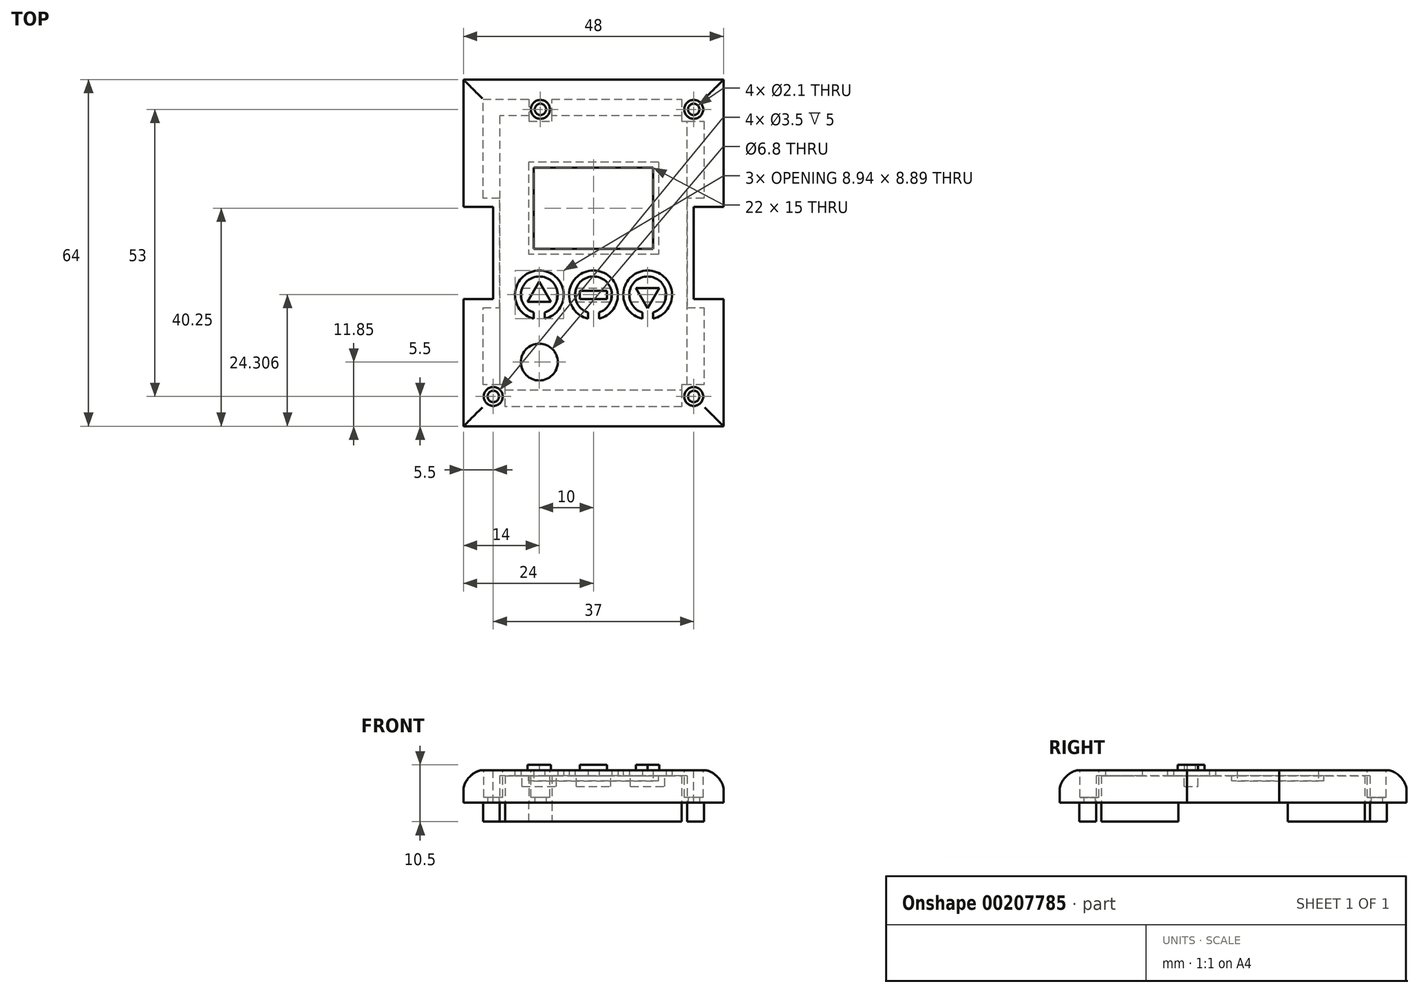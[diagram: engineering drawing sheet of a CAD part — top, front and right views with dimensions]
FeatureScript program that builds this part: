
annotation { "Feature Type Name" : "Feature", "Feature Type Description" : "" }
export const myFeature = defineFeature(function(context is Context, id is Id, definition is map)
    precondition{}
    {
        {
            var Q0;
            Q0=qCreatedBy(makeId("Top.planeOp"),FACE);
            var sketch = newSketch(context, id + "F0", { "sketchPlane" : qUnion([Q0])});
            skLineSegment(sketch, "E0.bottom", {"start": v(24, 32) * mm, "end": v(-24, 32) * mm});
            skLineSegment(sketch, "E0.top", {"start": v(24, -32) * mm, "end": v(-24, -32) * mm});
            skLineSegment(sketch, "E0.left", {"start": v(24, 32) * mm, "end": v(24, -32) * mm});
            skLineSegment(sketch, "E0.right", {"start": v(-24, 32) * mm, "end": v(-24, -32) * mm});
            skPoint(sketch, "E0.middle", {"position": v(0, 0) * mm});
            skSolve(sketch);
        }
        {
            var Q0;
            Q0 = qSketchRegion(id + "F0", true);
            extrude(context, id + "F1", {"entities" : qUnion([Q0]), "depth" : 6 * mm});
        }
        {
            var Q0;
            Q0=makeQuery(id+"F1.opExtrude","CAP_FACE",FACE,{"disambiguationData":[OSD([sQuery(id+"F0.wireOp",EDGE,"E0.bottom"),sQuery(id+"F0.wireOp",EDGE,"E0.top"),sQuery(id+"F0.wireOp",EDGE,"E0.left"),sQuery(id+"F0.wireOp",EDGE,"E0.right")])],"isStart":false});
            var sketch = newSketch(context, id + "F2", { "sketchPlane" : qUnion([Q0])});
            skLineSegment(sketch, "E1.bottom", {"start": v(-24, 8.5) * mm, "end": v(-18.5, 8.5) * mm});
            skLineSegment(sketch, "E1.top", {"start": v(-24, -8.5) * mm, "end": v(-18.5, -8.5) * mm});
            skLineSegment(sketch, "E1.left", {"start": v(-24, 8.5) * mm, "end": v(-24, -8.5) * mm});
            skLineSegment(sketch, "E1.right", {"start": v(-18.5, 8.5) * mm, "end": v(-18.5, -8.5) * mm});
            skPoint(sketch, "E1.middle", {"position": v(-21.25, 0) * mm});
            skLineSegment(sketch, "E2.bottom", {"start": v(24, 8.5) * mm, "end": v(18.5, 8.5) * mm});
            skLineSegment(sketch, "E2.top", {"start": v(24, -8.5) * mm, "end": v(18.5, -8.5) * mm});
            skLineSegment(sketch, "E2.left", {"start": v(24, 8.5) * mm, "end": v(24, -8.5) * mm});
            skLineSegment(sketch, "E2.right", {"start": v(18.5, 8.5) * mm, "end": v(18.5, -8.5) * mm});
            skPoint(sketch, "E2.middle", {"position": v(21.25, 0) * mm});
            skSolve(sketch);
        }
        {
            var Q0;
            Q0 = qSketchRegion(id + "F2", true);
            extrude(context, id + "F3", {"entities" : qUnion([Q0]), "operationType" : NewBodyOperationType.REMOVE, "endBound" : BoundingType.THROUGH_ALL, "oppositeDirection" : true, "depth" : 25 * mm});
        }
        {
            var Q0;
            Q0=makeQuery(id+"F1.opExtrude","CAP_FACE",FACE,{"disambiguationData":[OSD([sQuery(id+"F0.wireOp",EDGE,"E0.bottom"),sQuery(id+"F0.wireOp",EDGE,"E0.top"),sQuery(id+"F0.wireOp",EDGE,"E0.left"),sQuery(id+"F0.wireOp",EDGE,"E0.right")])],"isStart":true});
            var sketch = newSketch(context, id + "F4", { "sketchPlane" : qUnion([Q0])});
            skLineSegment(sketch, "E3", {"start": v(-20.4, -28.4) * mm, "end": v(-11.9, -28.4) * mm});
            skLineSegment(sketch, "E4", {"start": v(-11.9, -28.4) * mm, "end": v(-11.9, -24.3) * mm});
            skLineSegment(sketch, "E5", {"start": v(-11.9, -24.3) * mm, "end": v(-7.7, -24.3) * mm});
            skLineSegment(sketch, "E6", {"start": v(-7.7, -24.3) * mm, "end": v(-7.7, -28.4) * mm});
            skLineSegment(sketch, "E7", {"start": v(-7.7, -28.4) * mm, "end": v(16.3, -28.4) * mm});
            skLineSegment(sketch, "E8", {"start": v(16.3, -28.4) * mm, "end": v(16.3, -24.3) * mm});
            skLineSegment(sketch, "E9", {"start": v(16.3, -24.3) * mm, "end": v(20.4, -24.3) * mm});
            skLineSegment(sketch, "E10", {"start": v(20.4, -24.3) * mm, "end": v(20.4, -10.1) * mm});
            skLineSegment(sketch, "E11", {"start": v(20.4, -10.1) * mm, "end": v(15.5, -10.1) * mm});
            skLineSegment(sketch, "E12", {"start": v(15.5, -10.1) * mm, "end": v(15.5, 10.1) * mm});
            skLineSegment(sketch, "E13", {"start": v(15.5, 10.1) * mm, "end": v(20.4, 10.1) * mm});
            skLineSegment(sketch, "E14", {"start": v(20.4, 10.1) * mm, "end": v(20.4, 24.3) * mm});
            skLineSegment(sketch, "E15", {"start": v(20.4, 24.3) * mm, "end": v(16.3, 24.3) * mm});
            skLineSegment(sketch, "E16", {"start": v(16.3, 24.3) * mm, "end": v(16.3, 28.4) * mm});
            skLineSegment(sketch, "E17", {"start": v(16.3, 28.4) * mm, "end": v(-16.3, 28.4) * mm});
            skLineSegment(sketch, "E18", {"start": v(-16.3, 28.4) * mm, "end": v(-16.3, 24.3) * mm});
            skLineSegment(sketch, "E19", {"start": v(-16.3, 24.3) * mm, "end": v(-20.4, 24.3) * mm});
            skLineSegment(sketch, "E20", {"start": v(-20.4, 24.3) * mm, "end": v(-20.4, 10.1) * mm});
            skLineSegment(sketch, "E21", {"start": v(-20.4, 10.1) * mm, "end": v(-15.5, 10.1) * mm});
            skLineSegment(sketch, "E22", {"start": v(-15.5, 10.1) * mm, "end": v(-15.5, -10.1) * mm});
            skLineSegment(sketch, "E23", {"start": v(-15.5, -10.1) * mm, "end": v(-20.4, -10.1) * mm});
            skLineSegment(sketch, "E24", {"start": v(-20.4, -10.1) * mm, "end": v(-20.4, -28.4) * mm});
            skSolve(sketch);
        }
        {
            var Q0;
            Q0 = qSketchRegion(id + "F4", true);
            extrude(context, id + "F5", {"entities" : qUnion([Q0]), "operationType" : NewBodyOperationType.ADD, "depth" : 3.5 * mm});
        }
        {
            var Q0;
            Q0=makeQuery(id+"F5.opExtrude","CAP_FACE",FACE,{"disambiguationData":[OSD([sQuery(id+"F4.wireOp",EDGE,"E3"),sQuery(id+"F4.wireOp",EDGE,"E4"),sQuery(id+"F4.wireOp",EDGE,"E5"),sQuery(id+"F4.wireOp",EDGE,"E6"),sQuery(id+"F4.wireOp",EDGE,"E7"),sQuery(id+"F4.wireOp",EDGE,"E8"),sQuery(id+"F4.wireOp",EDGE,"E9"),sQuery(id+"F4.wireOp",EDGE,"E10"),sQuery(id+"F4.wireOp",EDGE,"E11"),sQuery(id+"F4.wireOp",EDGE,"E12"),sQuery(id+"F4.wireOp",EDGE,"E13"),sQuery(id+"F4.wireOp",EDGE,"E14"),sQuery(id+"F4.wireOp",EDGE,"E15"),sQuery(id+"F4.wireOp",EDGE,"E16"),sQuery(id+"F4.wireOp",EDGE,"E17"),sQuery(id+"F4.wireOp",EDGE,"E18"),sQuery(id+"F4.wireOp",EDGE,"E19"),sQuery(id+"F4.wireOp",EDGE,"E20"),sQuery(id+"F4.wireOp",EDGE,"E21"),sQuery(id+"F4.wireOp",EDGE,"E22"),sQuery(id+"F4.wireOp",EDGE,"E23"),sQuery(id+"F4.wireOp",EDGE,"E24")])],"isStart":false});
            var sketch = newSketch(context, id + "F6", { "sketchPlane" : qUnion([Q0])});
            skLineSegment(sketch, "E25", {"start": v(-16.3, 24.3) * mm, "end": v(-16.3, 25.3) * mm});
            skLineSegment(sketch, "E26", {"start": v(-16.3, 25.3) * mm, "end": v(16.3, 25.3) * mm});
            skLineSegment(sketch, "E27", {"start": v(16.3, 25.3) * mm, "end": v(16.3, 24.3) * mm});
            skLineSegment(sketch, "E28", {"start": v(16.3, 24.3) * mm, "end": v(17.3, 24.3) * mm});
            skPoint(sketch, "E29.endSnap0", {"position": v(17.95, 10.1) * mm});
            skLineSegment(sketch, "E30", {"start": v(17.3, 24.3) * mm, "end": v(17.3, -24.3) * mm});
            skLineSegment(sketch, "E31", {"start": v(17.3, -24.3) * mm, "end": v(16.3, -24.3) * mm});
            skLineSegment(sketch, "E32", {"start": v(16.3, -24.3) * mm, "end": v(16.3, -25.3) * mm});
            skLineSegment(sketch, "E33", {"start": v(16.3, -25.3) * mm, "end": v(-7.7, -25.3) * mm});
            skLineSegment(sketch, "E34", {"start": v(-7.7, -25.3) * mm, "end": v(-7.7, -24.3) * mm});
            skLineSegment(sketch, "E35", {"start": v(-7.7, -24.3) * mm, "end": v(-11.9, -24.3) * mm});
            skLineSegment(sketch, "E36", {"start": v(-11.9, -24.3) * mm, "end": v(-11.9, -25.3) * mm});
            skLineSegment(sketch, "E37", {"start": v(-11.9, -25.3) * mm, "end": v(-17.3, -25.3) * mm});
            skLineSegment(sketch, "E38", {"start": v(-17.3, -25.3) * mm, "end": v(-17.3, 24.3) * mm});
            skLineSegment(sketch, "E39", {"start": v(-17.3, 24.3) * mm, "end": v(-16.3, 24.3) * mm});
            skSolve(sketch);
        }
        {
            var Q0;
            Q0 = qSketchRegion(id + "F6", true);
            extrude(context, id + "F7", {"entities" : qUnion([Q0]), "operationType" : NewBodyOperationType.REMOVE, "oppositeDirection" : true, "depth" : 8.5 * mm});
        }
        {
            var Q0;
            Q0=makeQuery(id+"F1.opExtrude","CAP_FACE",FACE,{"disambiguationData":[OSD([sQuery(id+"F0.wireOp",EDGE,"E0.bottom"),sQuery(id+"F0.wireOp",EDGE,"E0.top"),sQuery(id+"F0.wireOp",EDGE,"E0.left"),sQuery(id+"F0.wireOp",EDGE,"E0.right")])],"isStart":true});
            var sketch = newSketch(context, id + "F8", { "sketchPlane" : qUnion([Q0])});
            skCircle(sketch, "E40", {"center": v(-18.5, 26.5) * mm, "radius": 1.05 * mm});
            skCircle(sketch, "E41", {"center": v(18.5, 26.5) * mm, "radius": 1.05 * mm});
            skCircle(sketch, "E42", {"center": v(18.5, -26.5) * mm, "radius": 1.05 * mm});
            skCircle(sketch, "E43", {"center": v(-9.8, -26.5) * mm, "radius": 1.05 * mm});
            skPoint(sketch, "E43.centerSnap0", {"position": v(-9.8, -24.3) * mm});
            skSolve(sketch);
        }
        {
            var Q0;
            Q0 = qSketchRegion(id + "F8", true);
            extrude(context, id + "F9", {"entities" : qUnion([Q0]), "operationType" : NewBodyOperationType.REMOVE, "endBound" : BoundingType.THROUGH_ALL, "oppositeDirection" : true, "depth" : 25 * mm});
        }
        {
            var Q0;
            Q0=makeQuery(id+"F1.opExtrude","CAP_FACE",FACE,{"disambiguationData":[OSD([sQuery(id+"F0.wireOp",EDGE,"E0.bottom"),sQuery(id+"F0.wireOp",EDGE,"E0.top"),sQuery(id+"F0.wireOp",EDGE,"E0.left"),sQuery(id+"F0.wireOp",EDGE,"E0.right")])],"isStart":false});
            var sketch = newSketch(context, id + "F10", { "sketchPlane" : qUnion([Q0])});
            skCircle(sketch, "E44", {"center": v(-9.8, 26.5) * mm, "radius": 1.75 * mm});
            skCircle(sketch, "E45", {"center": v(18.5, 26.5) * mm, "radius": 1.75 * mm});
            skCircle(sketch, "E46", {"center": v(18.5, -26.5) * mm, "radius": 1.75 * mm});
            skCircle(sketch, "E47", {"center": v(-18.5, -26.5) * mm, "radius": 1.75 * mm});
            skSolve(sketch);
        }
        {
            var Q0;
            Q0 = qSketchRegion(id + "F10", true);
            extrude(context, id + "F11", {"entities" : qUnion([Q0]), "operationType" : NewBodyOperationType.REMOVE, "oppositeDirection" : true, "depth" : 5 * mm});
        }
        {
            var Q0;
            Q0=makeQuery(id+"F7.boolean.opBoolean","COPY",FACE,{"derivedFrom":makeQuery(id+"F7.opExtrude","CAP_FACE",FACE,{"disambiguationData":[OSD([sQuery(id+"F6.wireOp",EDGE,"E25"),sQuery(id+"F6.wireOp",EDGE,"E26"),sQuery(id+"F6.wireOp",EDGE,"E27"),sQuery(id+"F6.wireOp",EDGE,"E28"),sQuery(id+"F6.wireOp",EDGE,"E30"),sQuery(id+"F6.wireOp",EDGE,"E31"),sQuery(id+"F6.wireOp",EDGE,"E32"),sQuery(id+"F6.wireOp",EDGE,"E33"),sQuery(id+"F6.wireOp",EDGE,"E34"),sQuery(id+"F6.wireOp",EDGE,"E35"),sQuery(id+"F6.wireOp",EDGE,"E36"),sQuery(id+"F6.wireOp",EDGE,"E37"),sQuery(id+"F6.wireOp",EDGE,"E38"),sQuery(id+"F6.wireOp",EDGE,"E39")])],"isStart":false})});
            var sketch = newSketch(context, id + "F12", { "sketchPlane" : qUnion([Q0])});
            skLineSegment(sketch, "E48.bottom", {"start": v(11, -0.75) * mm, "end": v(-11, -0.75) * mm});
            skLineSegment(sketch, "E48.top", {"start": v(11, -15.75) * mm, "end": v(-11, -15.75) * mm});
            skLineSegment(sketch, "E48.left", {"start": v(11, -0.75) * mm, "end": v(11, -15.75) * mm});
            skLineSegment(sketch, "E48.right", {"start": v(-11, -0.75) * mm, "end": v(-11, -15.75) * mm});
            skPoint(sketch, "E48.middle", {"position": v(0, -8.25) * mm});
            skSolve(sketch);
        }
        {
            var Q0;
            Q0 = qSketchRegion(id + "F12", true);
            extrude(context, id + "F13", {"entities" : qUnion([Q0]), "operationType" : NewBodyOperationType.REMOVE, "endBound" : BoundingType.THROUGH_ALL, "oppositeDirection" : true, "depth" : 25 * mm});
        }
        {
            var Q0;
            Q0=makeQuery(id+"F7.boolean.opBoolean","COPY",FACE,{"derivedFrom":makeQuery(id+"F7.opExtrude","CAP_FACE",FACE,{"disambiguationData":[OSD([sQuery(id+"F6.wireOp",EDGE,"E25"),sQuery(id+"F6.wireOp",EDGE,"E26"),sQuery(id+"F6.wireOp",EDGE,"E27"),sQuery(id+"F6.wireOp",EDGE,"E28"),sQuery(id+"F6.wireOp",EDGE,"E30"),sQuery(id+"F6.wireOp",EDGE,"E31"),sQuery(id+"F6.wireOp",EDGE,"E32"),sQuery(id+"F6.wireOp",EDGE,"E33"),sQuery(id+"F6.wireOp",EDGE,"E34"),sQuery(id+"F6.wireOp",EDGE,"E35"),sQuery(id+"F6.wireOp",EDGE,"E36"),sQuery(id+"F6.wireOp",EDGE,"E37"),sQuery(id+"F6.wireOp",EDGE,"E38"),sQuery(id+"F6.wireOp",EDGE,"E39")])],"isStart":false})});
            var sketch = newSketch(context, id + "F14", { "sketchPlane" : qUnion([Q0])});
            skArc(sketch, "E49", {"start": v(-1, 11) * mm, "mid": v(0, 4.35) * mm, "end": v(1, 11) * mm});
            skArc(sketch, "E50", {"start": v(-1, 12.14) * mm, "mid": v(0, 3.25) * mm, "end": v(1, 12.14) * mm});
            skLineSegment(sketch, "E51", {"start": v(-1, 12.14) * mm, "end": v(-1, 11) * mm});
            skLineSegment(sketch, "E52", {"start": v(1, 12.14) * mm, "end": v(1, 11) * mm});
            skArc(sketch, "E53", {"start": v(11, 11) * mm, "mid": v(10, 4.35) * mm, "end": v(9, 11) * mm});
            skArc(sketch, "E54", {"start": v(11, 12.14) * mm, "mid": v(10, 3.25) * mm, "end": v(9, 12.14) * mm});
            skLineSegment(sketch, "E55", {"start": v(11, 11) * mm, "end": v(11, 12.14) * mm});
            skLineSegment(sketch, "E56", {"start": v(9, 11) * mm, "end": v(9, 12.14) * mm});
            skArc(sketch, "E57", {"start": v(-9, 11) * mm, "mid": v(-10, 4.35) * mm, "end": v(-11, 11) * mm});
            skArc(sketch, "E58", {"start": v(-9, 12.14) * mm, "mid": v(-10, 3.25) * mm, "end": v(-11, 12.14) * mm});
            skLineSegment(sketch, "E59", {"start": v(-9, 11) * mm, "end": v(-9, 12.14) * mm});
            skLineSegment(sketch, "E60", {"start": v(-11, 12.14) * mm, "end": v(-11, 11) * mm});
            skSolve(sketch);
        }
        {
            var Q0;
            Q0 = qSketchRegion(id + "F14", true);
            extrude(context, id + "F15", {"entities" : qUnion([Q0]), "operationType" : NewBodyOperationType.REMOVE, "endBound" : BoundingType.THROUGH_ALL, "oppositeDirection" : true, "depth" : 25 * mm});
        }
        {
            var Q0;
            Q0=makeQuery(id+"F7.boolean.opBoolean","COPY",FACE,{"derivedFrom":makeQuery(id+"F7.opExtrude","CAP_FACE",FACE,{"disambiguationData":[OSD([sQuery(id+"F6.wireOp",EDGE,"E25"),sQuery(id+"F6.wireOp",EDGE,"E26"),sQuery(id+"F6.wireOp",EDGE,"E27"),sQuery(id+"F6.wireOp",EDGE,"E28"),sQuery(id+"F6.wireOp",EDGE,"E30"),sQuery(id+"F6.wireOp",EDGE,"E31"),sQuery(id+"F6.wireOp",EDGE,"E32"),sQuery(id+"F6.wireOp",EDGE,"E33"),sQuery(id+"F6.wireOp",EDGE,"E34"),sQuery(id+"F6.wireOp",EDGE,"E35"),sQuery(id+"F6.wireOp",EDGE,"E36"),sQuery(id+"F6.wireOp",EDGE,"E37"),sQuery(id+"F6.wireOp",EDGE,"E38"),sQuery(id+"F6.wireOp",EDGE,"E39")])],"isStart":false})});
            var sketch = newSketch(context, id + "F16", { "sketchPlane" : qUnion([Q0])});
            skLineSegment(sketch, "E61.bottom", {"start": v(-13.16, 9) * mm, "end": v(-6.84, 9) * mm});
            skLineSegment(sketch, "E61.top", {"start": v(-13.16, 6.5) * mm, "end": v(-6.84, 6.5) * mm});
            skLineSegment(sketch, "E61.left", {"start": v(-13.16, 9) * mm, "end": v(-13.16, 6.5) * mm});
            skLineSegment(sketch, "E61.right", {"start": v(-6.84, 9) * mm, "end": v(-6.84, 6.5) * mm});
            skLineSegment(sketch, "E62.bottom", {"start": v(-3.16, 9) * mm, "end": v(3.16, 9) * mm});
            skLineSegment(sketch, "E62.top", {"start": v(-3.16, 6.5) * mm, "end": v(3.16, 6.5) * mm});
            skLineSegment(sketch, "E62.left", {"start": v(-3.16, 9) * mm, "end": v(-3.16, 6.5) * mm});
            skLineSegment(sketch, "E62.right", {"start": v(3.16, 9) * mm, "end": v(3.16, 6.5) * mm});
            skLineSegment(sketch, "E63.bottom", {"start": v(6.84, 9) * mm, "end": v(13.16, 9) * mm});
            skLineSegment(sketch, "E63.top", {"start": v(6.84, 6.5) * mm, "end": v(13.16, 6.5) * mm});
            skLineSegment(sketch, "E63.left", {"start": v(6.84, 9) * mm, "end": v(6.84, 6.5) * mm});
            skLineSegment(sketch, "E63.right", {"start": v(13.16, 9) * mm, "end": v(13.16, 6.5) * mm});
            skSolve(sketch);
        }
        {
            var Q0;
            Q0 = qSketchRegion(id + "F16", true);
            extrude(context, id + "F17", {"entities" : qUnion([Q0]), "operationType" : NewBodyOperationType.ADD, "depth" : 2 * mm});
        }
        {
            var Q0;
            Q0=makeQuery(id+"F1.opExtrude","CAP_FACE",FACE,{"disambiguationData":[OSD([sQuery(id+"F0.wireOp",EDGE,"E0.bottom"),sQuery(id+"F0.wireOp",EDGE,"E0.top"),sQuery(id+"F0.wireOp",EDGE,"E0.left"),sQuery(id+"F0.wireOp",EDGE,"E0.right")])],"isStart":false});
            var sketch = newSketch(context, id + "F18", { "sketchPlane" : qUnion([Q0])});
            skCircle(sketch, "E64.cCircle", {"center": v(10, -7.75) * mm, "radius": 2.5 * mm, "construction": true});
            skLineSegment(sketch, "E64.0", {"start": v(10, -10.25) * mm, "end": v(7.83, -6.5) * mm});
            skLineSegment(sketch, "E64.1", {"start": v(7.83, -6.5) * mm, "end": v(12.17, -6.5) * mm});
            skLineSegment(sketch, "E64.2", {"start": v(12.17, -6.5) * mm, "end": v(10, -10.25) * mm});
            skCircle(sketch, "E65.cCircle", {"center": v(-10, -7.75) * mm, "radius": 2.5 * mm, "construction": true});
            skLineSegment(sketch, "E65.0", {"start": v(-12.17, -9) * mm, "end": v(-10, -5.25) * mm});
            skLineSegment(sketch, "E65.1", {"start": v(-10, -5.25) * mm, "end": v(-7.83, -9) * mm});
            skLineSegment(sketch, "E65.2", {"start": v(-7.83, -9) * mm, "end": v(-12.17, -9) * mm});
            skLineSegment(sketch, "E66.bottom", {"start": v(-2.5, -8.5) * mm, "end": v(2.5, -8.5) * mm});
            skLineSegment(sketch, "E66.top", {"start": v(-2.5, -7) * mm, "end": v(2.5, -7) * mm});
            skLineSegment(sketch, "E66.left", {"start": v(-2.5, -8.5) * mm, "end": v(-2.5, -7) * mm});
            skLineSegment(sketch, "E66.right", {"start": v(2.5, -8.5) * mm, "end": v(2.5, -7) * mm});
            skPoint(sketch, "E66.middle", {"position": v(0, -7.75) * mm});
            skSolve(sketch);
        }
        {
            var Q0;
            Q0 = qSketchRegion(id + "F18", true);
            extrude(context, id + "F19", {"entities" : qUnion([Q0]), "operationType" : NewBodyOperationType.ADD, "depth" : 1 * mm});
        }
        {
            var Q0;
            Q0=makeQuery(id+"F7.boolean.opBoolean","COPY",FACE,{"derivedFrom":makeQuery(id+"F7.opExtrude","CAP_FACE",FACE,{"disambiguationData":[OSD([sQuery(id+"F6.wireOp",EDGE,"E25"),sQuery(id+"F6.wireOp",EDGE,"E26"),sQuery(id+"F6.wireOp",EDGE,"E27"),sQuery(id+"F6.wireOp",EDGE,"E28"),sQuery(id+"F6.wireOp",EDGE,"E30"),sQuery(id+"F6.wireOp",EDGE,"E31"),sQuery(id+"F6.wireOp",EDGE,"E32"),sQuery(id+"F6.wireOp",EDGE,"E33"),sQuery(id+"F6.wireOp",EDGE,"E34"),sQuery(id+"F6.wireOp",EDGE,"E35"),sQuery(id+"F6.wireOp",EDGE,"E36"),sQuery(id+"F6.wireOp",EDGE,"E37"),sQuery(id+"F6.wireOp",EDGE,"E38"),sQuery(id+"F6.wireOp",EDGE,"E39")])],"isStart":false})});
            var sketch = newSketch(context, id + "F20", { "sketchPlane" : qUnion([Q0])});
            skLineSegment(sketch, "E67.bottom", {"start": v(-11, -0.75) * mm, "end": v(11, -0.75) * mm});
            skLineSegment(sketch, "E67.top", {"start": v(-11, -15.75) * mm, "end": v(11, -15.75) * mm});
            skLineSegment(sketch, "E67.left", {"start": v(-11, -0.75) * mm, "end": v(-11, -15.75) * mm});
            skLineSegment(sketch, "E67.right", {"start": v(11, -0.75) * mm, "end": v(11, -15.75) * mm});
            skLineSegment(sketch, "E68.bottom", {"start": v(12, -16.75) * mm, "end": v(-12, -16.75) * mm});
            skLineSegment(sketch, "E68.top", {"start": v(12, 0.25) * mm, "end": v(-12, 0.25) * mm});
            skLineSegment(sketch, "E68.left", {"start": v(12, -16.75) * mm, "end": v(12, 0.25) * mm});
            skLineSegment(sketch, "E68.right", {"start": v(-12, -16.75) * mm, "end": v(-12, 0.25) * mm});
            skSolve(sketch);
        }
        {
            var Q0;
            Q0 = qSketchRegion(id + "F20", true);
            extrude(context, id + "F21", {"entities" : qUnion([Q0]), "operationType" : NewBodyOperationType.ADD, "depth" : 1 * mm});
        }
        {
            var Q0;
            {var subQ0=sQuery(id+"F0.wireOp",EDGE,"E0.bottom");var subQ1=sQuery(id+"F0.wireOp",EDGE,"E0.left");Q0=makeQuery(id+"F3.boolean.opBoolean","SPLIT",EDGE,{"disambiguationData":[TD([makeQuery(id+"F1.opExtrude","SWEPT_FACE",FACE,{"disambiguationData":[OSD([subQ0])]})])],"derivedFrom":makeQuery(id+"F1.opExtrude","CAP_EDGE",EDGE,{"disambiguationData":[OSD([subQ1])],"isStart":false})});}
            var Q1;
            Q1=makeQuery(id+"F1.opExtrude","CAP_EDGE",EDGE,{"disambiguationData":[OSD([sQuery(id+"F0.wireOp",EDGE,"E0.bottom")])],"isStart":false});
            var Q2;
            {var subQ0=sQuery(id+"F0.wireOp",EDGE,"E0.bottom");var subQ1=sQuery(id+"F0.wireOp",EDGE,"E0.right");Q2=makeQuery(id+"F3.boolean.opBoolean","SPLIT",EDGE,{"disambiguationData":[TD([makeQuery(id+"F1.opExtrude","SWEPT_FACE",FACE,{"disambiguationData":[OSD([subQ0])]})])],"derivedFrom":makeQuery(id+"F1.opExtrude","CAP_EDGE",EDGE,{"disambiguationData":[OSD([subQ1])],"isStart":false})});}
            var Q3;
            {var subQ0=sQuery(id+"F0.wireOp",EDGE,"E0.right");var subQ1=sQuery(id+"F0.wireOp",EDGE,"E0.top");Q3=makeQuery(id+"F3.boolean.opBoolean","SPLIT",EDGE,{"disambiguationData":[TD([makeQuery(id+"F1.opExtrude","SWEPT_FACE",FACE,{"disambiguationData":[OSD([subQ1])]})])],"derivedFrom":makeQuery(id+"F1.opExtrude","CAP_EDGE",EDGE,{"disambiguationData":[OSD([subQ0])],"isStart":false})});}
            var Q4;
            Q4=makeQuery(id+"F1.opExtrude","CAP_EDGE",EDGE,{"disambiguationData":[OSD([sQuery(id+"F0.wireOp",EDGE,"E0.top")])],"isStart":false});
            var Q5;
            {var subQ0=sQuery(id+"F0.wireOp",EDGE,"E0.left");var subQ1=sQuery(id+"F0.wireOp",EDGE,"E0.top");Q5=makeQuery(id+"F3.boolean.opBoolean","SPLIT",EDGE,{"disambiguationData":[TD([makeQuery(id+"F1.opExtrude","SWEPT_FACE",FACE,{"disambiguationData":[OSD([subQ1])]})])],"derivedFrom":makeQuery(id+"F1.opExtrude","CAP_EDGE",EDGE,{"disambiguationData":[OSD([subQ0])],"isStart":false})});}
            fillet(context, id + "F22", {"entities" : qUnion([Q0, Q1, Q2, Q3, Q4, Q5]), "radius" : 3.5 * mm, "tangentPropagation" : true, "rho" : 0.33, "crossSection" : FilletCrossSection.CONIC, "allowEdgeOverflow" : false});
        }
        {
            var Q0;
            Q0=makeQuery(id+"F7.boolean.opBoolean","COPY",FACE,{"derivedFrom":makeQuery(id+"F7.opExtrude","CAP_FACE",FACE,{"disambiguationData":[OSD([sQuery(id+"F6.wireOp",EDGE,"E25"),sQuery(id+"F6.wireOp",EDGE,"E26"),sQuery(id+"F6.wireOp",EDGE,"E27"),sQuery(id+"F6.wireOp",EDGE,"E28"),sQuery(id+"F6.wireOp",EDGE,"E30"),sQuery(id+"F6.wireOp",EDGE,"E31"),sQuery(id+"F6.wireOp",EDGE,"E32"),sQuery(id+"F6.wireOp",EDGE,"E33"),sQuery(id+"F6.wireOp",EDGE,"E34"),sQuery(id+"F6.wireOp",EDGE,"E35"),sQuery(id+"F6.wireOp",EDGE,"E36"),sQuery(id+"F6.wireOp",EDGE,"E37"),sQuery(id+"F6.wireOp",EDGE,"E38"),sQuery(id+"F6.wireOp",EDGE,"E39")])],"isStart":false})});
            var sketch = newSketch(context, id + "F23", { "sketchPlane" : qUnion([Q0])});
            skCircle(sketch, "E69", {"center": v(-10, 20.15) * mm, "radius": 3.4 * mm});
            skSolve(sketch);
        }
        {
            var Q0;
            Q0 = qSketchRegion(id + "F23", true);
            extrude(context, id + "F24", {"entities" : qUnion([Q0]), "operationType" : NewBodyOperationType.REMOVE, "endBound" : BoundingType.THROUGH_ALL, "oppositeDirection" : true, "depth" : 25 * mm});
        }
    });
